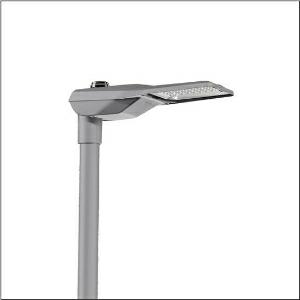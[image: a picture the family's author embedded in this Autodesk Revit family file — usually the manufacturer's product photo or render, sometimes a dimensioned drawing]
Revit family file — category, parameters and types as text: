
# Revit family: streetlight_sl_21_mini___p1_0a_5xe6a37n08gb_7347
name_source: partatom
category: Lighting Fixtures
units: mm (PartAtom-declared; Revit-internal decimal feet)

## family parameters
Cut with Voids When Loaded = No
Host = Face
Light Source = No
Part Type = Normal
Room Calculation Point = No
Round Connector Dimension = Use Diameter
Shared = No

## types (1)
- --- (1 x LED, 5940 lm, 40.4 W, 3000K)
    Apparent Load = 40 VA
    CIE Flux Codes = 21 50 90 100 100
    Color Rendering = 70
    Color Temperature = 3000K
    Default Elevation = 1800 mm
    Description = Streetlight SL 21 mini, mast luminaire, primary light control with lens, of PMMA, primary optical cover: cover, of toughened safety glass, transparent, light distribution: P1.0a, light emission: direct distribution, primary light characteristic: asymmetric, installation type: side-entry, LED, 3G 1.5mm², High Power LED, rated luminous flux: 5.940lm, luminous efficacy: 147lm/W, light colour: 730, colour temperature: 3000K, control gear: NEMA (7pin), control: overheat protection, pre-setting: linear dimming characteristic, constant luminous flux control, time-dependent luminous flux control, flexible luminous flux parameterisation, mains connection: 230..240V, AC, 50/60Hz, connection cable pre-assembled, cable length: 8,5m, wiring characteristics: H07RN-F, start of lifetime: 40W, end of service life: 41W, reduction: 19W, luminaire housing, of diecast aluminium (EN AC-44300), powder-coated, Siteco® metallic grey (DB 702S), corrosivity category C5 mid according to DIN EN ISO 12944, multi-level sealing system, sealing non-destructively replaceable, inclination adjustable: 0°, 5°, 10°, 15°, length: 628mm, width: 235mm, height: 110mm, spigot size: 42mm (side-entry), mounting height: 4..8m, protection rating (complete): IP66, insulation class (complete): insulation class I (protective earthing), certification: CE, ENEC, ENEC+, VDE, impact resistance: IK10, permissible operating ambient temperature for outdoor applications: -40..+50°C, standard-compliant lighting for roads and squares, packaging unit: 1 piece

Light Distribution: P1.0a
    Height = 110 mm
    Lamp = 1 x LED
    Lamp Light Flux = 5940 lm
    Lamp Power = 40.4 W
    Lamp count = 1
    Length = 625 mm
    Luminous efficacy = 147 lm/W
    Manufacturer = Siteco
    ModVariant = No
    Model = 5XE6A37N08GB
    Number of Poles = 1
    OnlyDefault = Yes
    Power Factor = 1
    Product Name = Streetlight SL 21 mini | P1.0a
    Product group = mast luminaire | pylon top
    ProductGroupID = 6100
    Protection Class = Protection class I
    Protection Degree = IP 66
    RLX_Detail_Level = 1
    RLX_Emergency_Light_Flux = 0 lm
    RLX_Emergency_Type = 0
    RLX_Emergency_Type_DB = No
    RlxData = <blob elided: 37037 chars, md5=49bd7701>
    Socket = socket
    Standby Power = 0 W
    System Light Flux = 5940 lm
    System Power = 40 W
    Type Comments = factory setting: luminous flux: 100 % | dim-lin: 254 | 812 mA
    Type Image = l_1294379.jpg
    URL = http://relux.com
    VarID = @adj_134718
    Voltage = 0 V
    Weight = 0.00 kg
    Width = 234 mm

## geometry (parser evidence)
native form markers: Blend x4, Sweep x12
no freeform markers — native parametric forms only
